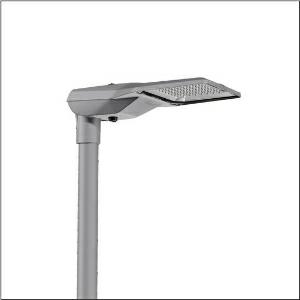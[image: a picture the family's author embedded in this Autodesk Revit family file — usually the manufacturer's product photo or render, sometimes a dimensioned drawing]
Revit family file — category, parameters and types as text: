
# Revit family: streetlight_sl_21_midi___stw1_0a_5xe3e23t08lb_dab2
name_source: partatom
category: Lighting Fixtures
units: mm (PartAtom-declared; Revit-internal decimal feet)

## family parameters
Cut with Voids When Loaded = No
Host = Face
Light Source = No
Part Type = Normal
Room Calculation Point = No
Round Connector Dimension = Use Diameter
Shared = No

## types (1)
- --- (1 x LED, 11880 lm, 99.6 W, 2200K)
    Apparent Load = 100 VA
    CIE Flux Codes = 38 75 98 100 100
    Color Rendering = 70
    Color Temperature = 2200K
    Default Elevation = 1800 mm
    Description = Streetlight SL 21 midi, mast luminaire, primary light control with lens, of PMMA, primary optical cover: cover, of toughened safety glass, transparent, light distribution: STW1.0a, light emission: direct distribution, primary light characteristic: asymmetric, installation type: side-entry, post-top, LED, High Power LED, rated luminous flux: 11.880lm, luminous efficacy: 119lm/W, light colour: 722, colour temperature: 2200K, control gear: D4i, control: overheat protection, constant luminous flux control, time-dependent luminous flux control, flexible luminous flux parameterisation, pre-setting: logarithmic dimming characteristic, mains connection: 230..240V, AC, 50/60Hz, start of lifetime: 100W, end of service life: 102W, reduction: 45W, luminaire housing, of diecast aluminium, powder-coated, SITECO metallic grey (DB 702S), corrosivity category C5 high according to DIN EN ISO 12944, please order mast flange separately, inclination adjustable: 0°, 5°, 10°, 15°, sealing non-destructively replaceable, multi-level sealing system, length: 644mm, width: 335mm, height: 110mm, mast flange for spigot size: 42mm (side-entry): 5XC10008XM4, 60/48mm (side-entry/post-top): 5XC10108XM2, 76/60mm (side-entry/post-top): 5XC10108XM1, mounting height: 4..8m, Smart Interface below and above, protection rating (complete): IP66, insulation class (complete): insulation class II (safety insulation), certification: CE, ENEC, ENEC+, VDE, impact resistance: IK10, permissible operating ambient temperature for outdoor applications: -40..+50°C, standard-compliant lighting for roads and squares, packaging unit: 1 piece

Light Distribution: STW1.0a
    Height = 111 mm
    Lamp = 1 x LED
    Lamp Light Flux = 11880 lm
    Lamp Power = 99.6 W
    Lamp count = 1
    Length = 644 mm
    Luminous efficacy = 119 lm/W
    Manufacturer = Siteco
    ModVariant = No
    Model = 5XE3E23T08LB
    Number of Poles = 1
    OnlyDefault = Yes
    Power Factor = 1
    Product Name = Streetlight SL 21 midi | STW1.0a
    Product group = mast luminaire | pylon top
    ProductGroupID = 6100
    Protection Class = Protection class II
    Protection Degree = IP 66
    RLX_Detail_Level = 1
    RLX_Emergency_Light_Flux = 0 lm
    RLX_Emergency_Type = 0
    RLX_Emergency_Type_DB = No
    RlxData = <blob elided: 26993 chars, md5=6daae473>
    Socket = socket
    Standby Power = 0 W
    System Light Flux = 11880 lm
    System Power = 100 W
    Type Comments = factory setting: luminous flux: 100 % | dim-lin: 254 | 1020 mA
    Type Image = l_1004304.jpg
    URL = http://relux.com
    VarID = @adj_031577
    Voltage = 0 V
    Weight = 0.00 kg
    Width = 336 mm

## geometry (parser evidence)
native form markers: Blend x4, Sweep x11
no freeform markers — native parametric forms only
